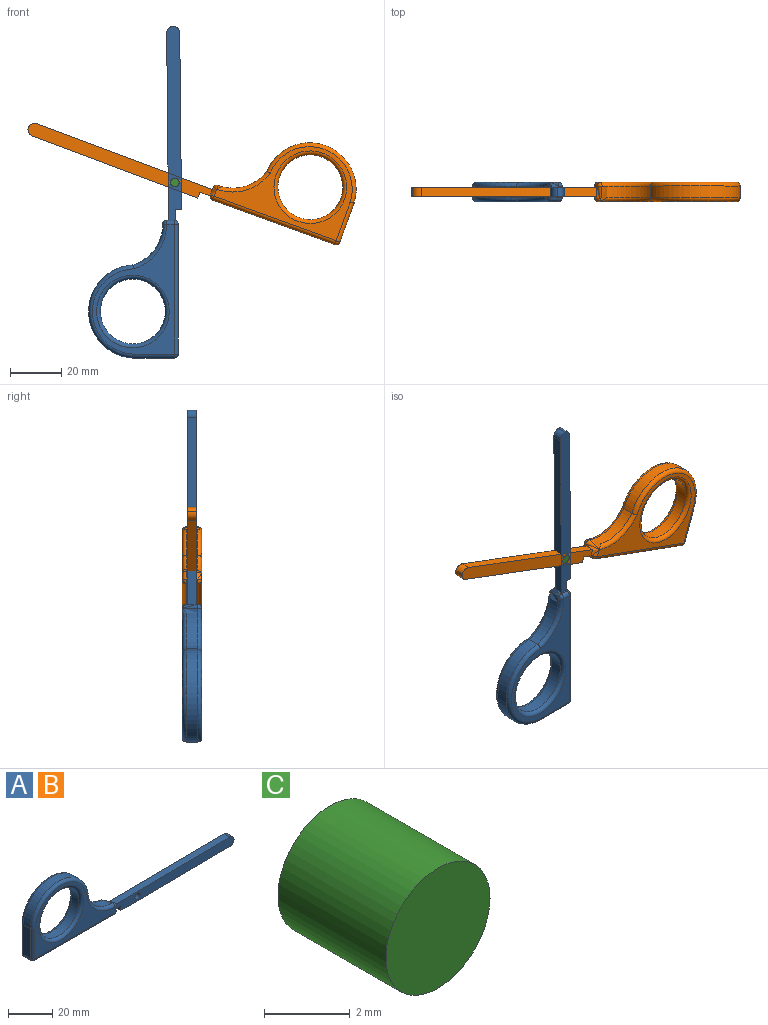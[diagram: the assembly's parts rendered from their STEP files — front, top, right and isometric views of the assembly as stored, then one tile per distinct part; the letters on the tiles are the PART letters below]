
ASSEMBLY  parts=3 mates=2
PART A: 37 faces, bbox 133.6x9.6x39.9 mm
  f0: plane 8.04x4.97mm, normal (1,0,0), area 10.4mm2, adj f1,f2,f16,f18,f19,f23,f34
  f1: cylinder r=1.52mm len=4.57mm, axis (0,1,0), area 9.5mm2, adj f0,f7,f11,f18,f19,f25,f35
  f2: cylinder r=1.52mm len=6.1mm, axis (0,1,0), area 14.6mm2, adj f0,f3,f32
  f3: cylinder r=16.51mm len=16mm, axis (0,1,0), area 97.2mm2, adj f2,f4,f20,f30
  f4: cylinder r=18.25mm len=36.45mm, axis (0,1,0), area 254mm2, adj f3,f5,f21,f28
  f5: plane 16.26x4.57mm, normal (-1,0,0), area 74.3mm2, adj f4,f6,f22,f29
  f6: cylinder r=1.52mm len=4.57mm, axis (0,1,0), area 10.9mm2, adj f5,f7,f24,f31
  f7: plane 50.93x4.57mm, normal (0,0,-1), area 232.8mm2, adj f1,f6,f26,f33
  f8: cylinder r=12.7mm len=25.4mm, axis (0,1,0), area 364.8mm2, adj f27,f36
  f9: plane 50.93x32.09mm, normal (0,-1,0), area 429.4mm2, adj f28,f29,f30,f33,f34,f36
  f10: plane 50.93x32.09mm, normal (0,1,0), area 429.4mm2, adj f20,f21,f22,f23,f26,f27
  f11: plane 4.32x3.56mm, normal (0.01,0,-1), area 15.4mm2, adj f1,f12,f18,f19
  f12: plane 3.56x2.45mm, normal (-1,0,0), area 8.7mm2, adj f11,f13,f18,f19
  f13: plane 69.08x3.56mm, normal (0.01,0,-1), area 245.7mm2, adj f12,f14,f18,f19
  f14: cylinder r=2.79mm len=3.56mm, axis (0,1,0), area 14.8mm2, adj f13,f15,f18,f19
  f15: cylinder r=2.79mm len=3.56mm, axis (0,1,0), area 15.1mm2, adj f14,f16,f18,f19
  f16: plane 73.26x3.56mm, normal (-0.01,0,1), area 260.5mm2, adj f0,f15,f18,f19
  f17: cylinder r=1.72mm len=3.56mm, axis (0,1,0), area 38.5mm2, adj f18,f19
  f18: plane 76.19x5.81mm, normal (0,-1,0), area 367.1mm2, adj f0,f1,f11,f12,f13,f14,f15,f16
  f19: plane 76.19x5.81mm, normal (0,1,0), area 367.1mm2, adj f0,f1,f11,f12,f13,f14,f15,f16
  f20: torus R=18.03mm, axis (0,-1,0), area -0.2mm2, adj f3,f10,f21
  f21: torus R=16.72mm, axis (0,-1,0), area 129.1mm2, adj f4,f10,f20,f22
  f22: cylinder r=1.52mm len=16.26mm, axis (0,0,-1), area 38.9mm2, adj f5,f10,f21,f24
  f23: cylinder r=1.52mm len=3.03mm, axis (0,0,1), area 7.3mm2, adj f0,f10,f25
  f24: sphere r=1.52mm, area 5mm2, adj f6,f22,f26
  f25: sphere r=1.52mm, area 2.3mm2, adj f1,f23,f26
  f26: cylinder r=1.52mm len=50.93mm, axis (1,0,0), area 121.9mm2, adj f7,f10,f24,f25
  f27: torus R=14.22mm, axis (0,-1,0), area 199.4mm2, adj f8,f10
  f28: torus R=16.72mm, axis (0,-1,0), area 129.1mm2, adj f4,f9,f29,f30
  f29: cylinder r=1.52mm len=16.26mm, axis (0,0,1), area 38.9mm2, adj f5,f9,f28,f31
  f30: torus R=18.03mm, axis (0,-1,0), area 52.8mm2, adj f3,f9,f28,f32
  f31: sphere r=1.52mm, area 3.6mm2, adj f6,f29,f33
  f32: sphere r=1.52mm, area 5mm2, adj f2,f30,f34
  f33: cylinder r=1.52mm len=50.93mm, axis (-1,0,0), area 121.9mm2, adj f7,f9,f31,f35
  f34: cylinder r=1.52mm len=3.03mm, axis (0,0,-1), area 7.3mm2, adj f0,f9,f32,f35
  f35: sphere r=1.52mm, area 2.3mm2, adj f1,f33,f34
  f36: torus R=14.22mm, axis (0,-1,0), area 199.4mm2, adj f8,f9
PART B: same geometry as A
PART C: 3 faces, bbox 3.4x3.6x3.4 mm
  f0: cylinder r=1.71mm len=3.56mm, axis (0,1,0), area 38.3mm2, adj f1,f2
  f1: plane 3.43x3.43mm, normal (0,-1,0), area 9.2mm2, adj f0
  f2: plane 3.43x3.43mm, normal (0,1,0), area 9.2mm2, adj f0
PLACE A rot(axis=(0,-1,0),90deg) t=(-48.03,24.3,-72.5)mm
PLACE B rot(axis=(0.17,0,0.98),180deg) t=(5.51,24.3,-35)mm
PLACE C rot(axis=(0,1,0),20deg) t=(-43.52,26.08,-21.95)mm
MATE revolute B.f17 <-> A.f17  axis (0,1,0) through (-43.52,26.08,-21.95)mm
MATE slider C.f0 <-> B.f17  axis (0,1,0) through (-43.52,26.08,-21.95)mm
